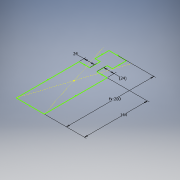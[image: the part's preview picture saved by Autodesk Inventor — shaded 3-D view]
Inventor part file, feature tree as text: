
AUTODESK INVENTOR PART (.ipt)
format: ipt  version: 2018 (Build 220112000, 112)  size: 94,208 bytes
history: native  units: mm
features: sketch x1
ambient origin geometry x8: Origin, YZ Plane, XZ Plane, XY Plane, X Axis, Y Axis, Z Axis, Center Point
feature tree (1):
  sketch  "Boceto1"  dims[d6=200.0mm d7=144.0mm d8=24.0mm d9=24.0mm]
